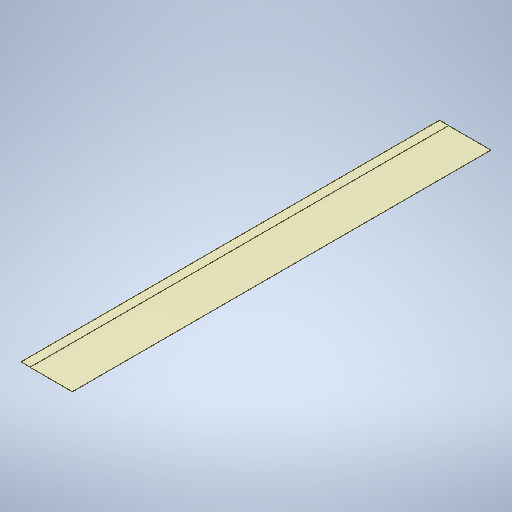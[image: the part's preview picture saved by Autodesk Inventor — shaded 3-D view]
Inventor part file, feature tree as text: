
AUTODESK INVENTOR PART (.ipt)
format: ipt  version: 2025 (Build 290162010, 162A)  size: 250,880 bytes
history: native  units: in
note: dims shown in document units (in); Inventor stores cm internally (conversion verified against a paired STEP export)
features: extrude x1, sketch x1
ambient origin geometry x8: Origin, YZ Plane, XZ Plane, XY Plane, X Axis, Y Axis, Z Axis, Center Point
bodies: Solid1 (feature_tree)
feature tree (2):
  extrude  "Extrusion1"  Depth=0.125in
  sketch  "Sketch1"  dims[d0=6.25in d1=0.125in d2=0.125in d3=0.125in d4=0.125in d5=29.625in d6=292.512in d7=0.0in]
